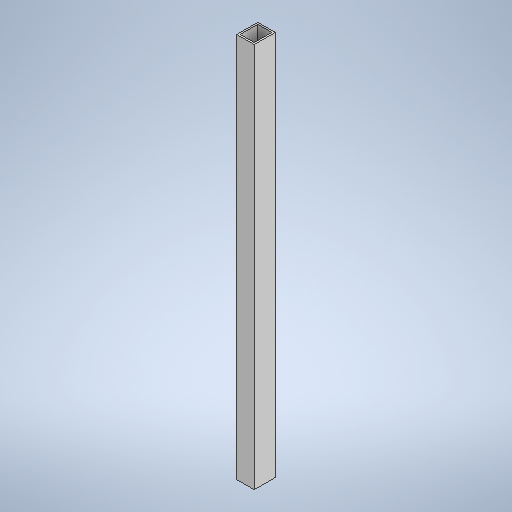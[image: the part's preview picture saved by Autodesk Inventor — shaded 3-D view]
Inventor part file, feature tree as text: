
AUTODESK INVENTOR PART (.ipt)
format: ipt  version: 2025 (Build 290162000, 162)  size: 257,024 bytes
history: native  units: in
note: dims shown in document units (in); Inventor stores cm internally (conversion verified against a paired STEP export)
features: extrude x2, sketch x2
ambient origin geometry x8: Origin, YZ Plane, XZ Plane, XY Plane, X Axis, Y Axis, Z Axis, Center Point
bodies: Solid1 (feature_tree)
feature tree (4):
  extrude  "Extrusion1"  Depth=0.9843in
  extrude  "Extrusion2"  Depth=0.9843in
  sketch  "Sketch1"  dims[d0=1.1811in d1=0.9843in]
  sketch  "Sketch2"  dims[d2=21.6535in d3=0.0in d4=0.9843in d5=0.7874in d6=23.622in d7=0.0in]
